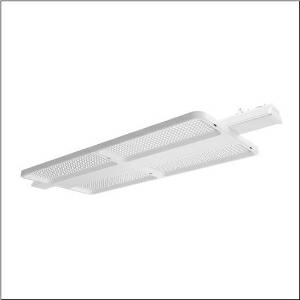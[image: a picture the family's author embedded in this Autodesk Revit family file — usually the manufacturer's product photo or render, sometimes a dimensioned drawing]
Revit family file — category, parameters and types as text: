
# Revit family: highbay_21_fur_licross_r__tragschiene_maxi_52hn12db4qla_5cb2
name_source: partatom
category: Lighting Fixtures
units: mm (PartAtom-declared; Revit-internal decimal feet)

## family parameters
Cut with Voids When Loaded = No
Host = Face
Light Source = No
Part Type = Normal
Room Calculation Point = No
Round Connector Dimension = Use Diameter
Shared = No

## types (1)
- --- (1 x LED, 38000 lm, 197.7 W, 4000K)
    Apparent Load = 198 VA
    CIE Flux Codes = 90 98 100 100 100
    Color Rendering = 80
    Color Temperature = 4000K
    Default Elevation = 1800 mm
    Description = high bay luminaire Highbay 21 for Licross trunking rail maxi; direct symmetric wide distribution, light control with lens of PMMA; UGR ≤ 22 (X = 4H | Y = 8H | S = 0.25H | reflection values 70/50/20); luminous flux: 38.000lm; light colour: 840, colour temperature: 4000K, MacAdam ≤ 3 SDCM (initial), colour rendering: CRI > 80; luminous efficacy: 192,2lm/W; rated service life: 75.000h (L80) at AT= ta max; control: DALI 2; luminaire connection: plug, 5-pole, with phase selectionmains connection: 230..240V, AC 50/60Hz; connected load: 197,7W; protection rating (complete): IP64; insulation class (complete): insulation class I (protective earthing); protection symbol: D; impact resistance: IK06; certification: CE, ENEC, VDE, UKCA; internal wiring halogen-free; luminaire LABS conformity tested according to VDMA 24364:2018-05; Suitable for use in the food industry according to the specifications of IFS-Food, HACCP and/or BRC; housing frame of high-performance plastic PA6, matt traffic white (RAL 9016); cover of PMMA; fixing on rail side of steel, galvanised, white; blank cover of PC/ABS, traffic white (RAL 9016); dimension (LxWxH): 1.250 x 442 x 71mm; permissible operating ambient temperature: -40..+55°C (reducing of maximum allowable ambient temperature of 5°C with ceiling mounting); packaging unit: 1 piece
    Height = 72 mm  [stored 0.23622 ft]
    Lamp = 1 x LED
    Lamp Light Flux = 38000 lm
    Lamp Power = 197.7 W
    Lamp count = 1
    Length = 946 mm
    Luminous efficacy = 192 lm/W
    Manufacturer = Siteco
    ModVariant = No
    Model = 52HN12DB4QLA
    Mounting Place = Ceiling
    Mounting Type = Pendant
    Number of Poles = 1
    OnlyDefault = Yes
    Power Factor = 1
    Product Name = Highbay 21 für Licross® Tragschiene maxi
    Product group = high bay luminaire
    ProductGroupID = 902
    Protection Class = Protection class I
    Protection Degree = IP 64
    RLX_Detail_Level = 1
    RLX_Emergency_Light_Flux = 0 lm
    RLX_Emergency_Type = 0
    RLX_Emergency_Type_DB = No
    RlxData = <blob elided: 130513 chars, md5=8f9f7bd6>
    Socket = socket
    Standby Power = 0 W
    System Light Flux = 38000 lm
    System Power = 198 W
    Type Comments = factory setting: luminous flux: 100 % | dim-lin: 254 | 918 mA
    Type Image = l_1361711.jpg
    URL = http://relux.com
    VarID = @adj_017451
    Voltage = 0 V
    Weight = 0.00 kg
    Width = 442 mm

note: [stored X ft] marks values corroborated as IEEE doubles in the binary element streams (Revit-internal decimal feet)

## geometry (parser evidence)
native form markers: Blend x4, Sweep x10
no freeform markers — native parametric forms only
